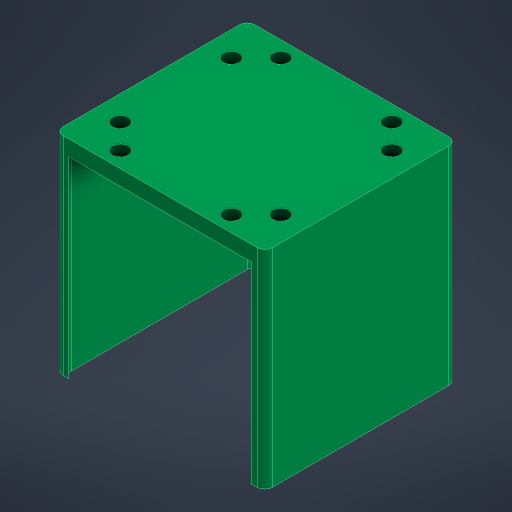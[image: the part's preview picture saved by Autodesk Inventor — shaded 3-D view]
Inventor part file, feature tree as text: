
AUTODESK INVENTOR PART (.ipt)
format: ipt  version: 2023.4 (Build 274418000, 418)  size: 231,936 bytes
history: native  units: mm
features: extrude x5, other x4, sketch x3, plane x2, reference x2, fillet x1, mirror x1, projected_geometry x1
ambient origin geometry x8: Origin, YZ Plane, XZ Plane, XY Plane, X Axis, Y Axis, Z Axis, Center Point
bodies: Solid1 (feature_tree)
feature tree (19):
  sketch  "Sketch1"  dims[d0=4.0mm d1=0.0mm d3=4.25mm]
  plane  "Work Plane1"
  extrude  "Extrusion1"  Depth=4.0mm
  sketch  "Sketch2"  dims[d4=2.125mm d5=2.0mm d6=0.0mm]
  extrude  "Extrusion2"  Depth=2.0mm TaperAngle=0.0deg
  extrude  "Extrusion3"  Depth=49.8mm TaperAngle=0.0deg
  extrude  "Extrusion4"  Depth=2.0mm
  fillet  "Fillet1"  Radius=5.0mm
  extrude  "Extrusion5"  Depth=49.8mm TaperAngle=0.0deg
  plane  "Work Plane2"
  mirror  "Mirror1"
  reference  "Reference1"
  projected_geometry  "Projected Loop1"
  sketch  "Sketch3"  dims[d7=2.0mm d8=0.0mm d9=49.8mm d10=0.0mm d11=2.0mm d12=5.0mm d13=49.8mm d14=0.0mm d15=0.125mm d16=-24.875mm]
  reference  "Reference2"
  other  "<path>\Projects\Project Protocube\Protocube\CAD, STL, OBJ Files\1 CAD\Cube 1x1 V5.iam"
  other  "Cube 1x1 V5.iam"
  other  "Cube 1x1 Top V5 Closed Slotted:1"
  other  "Cube 1x1 Bottom V5 Closed Slotted:1"
note: 1 file-system path scrubbed to <path> (originals preserved in map.json)
